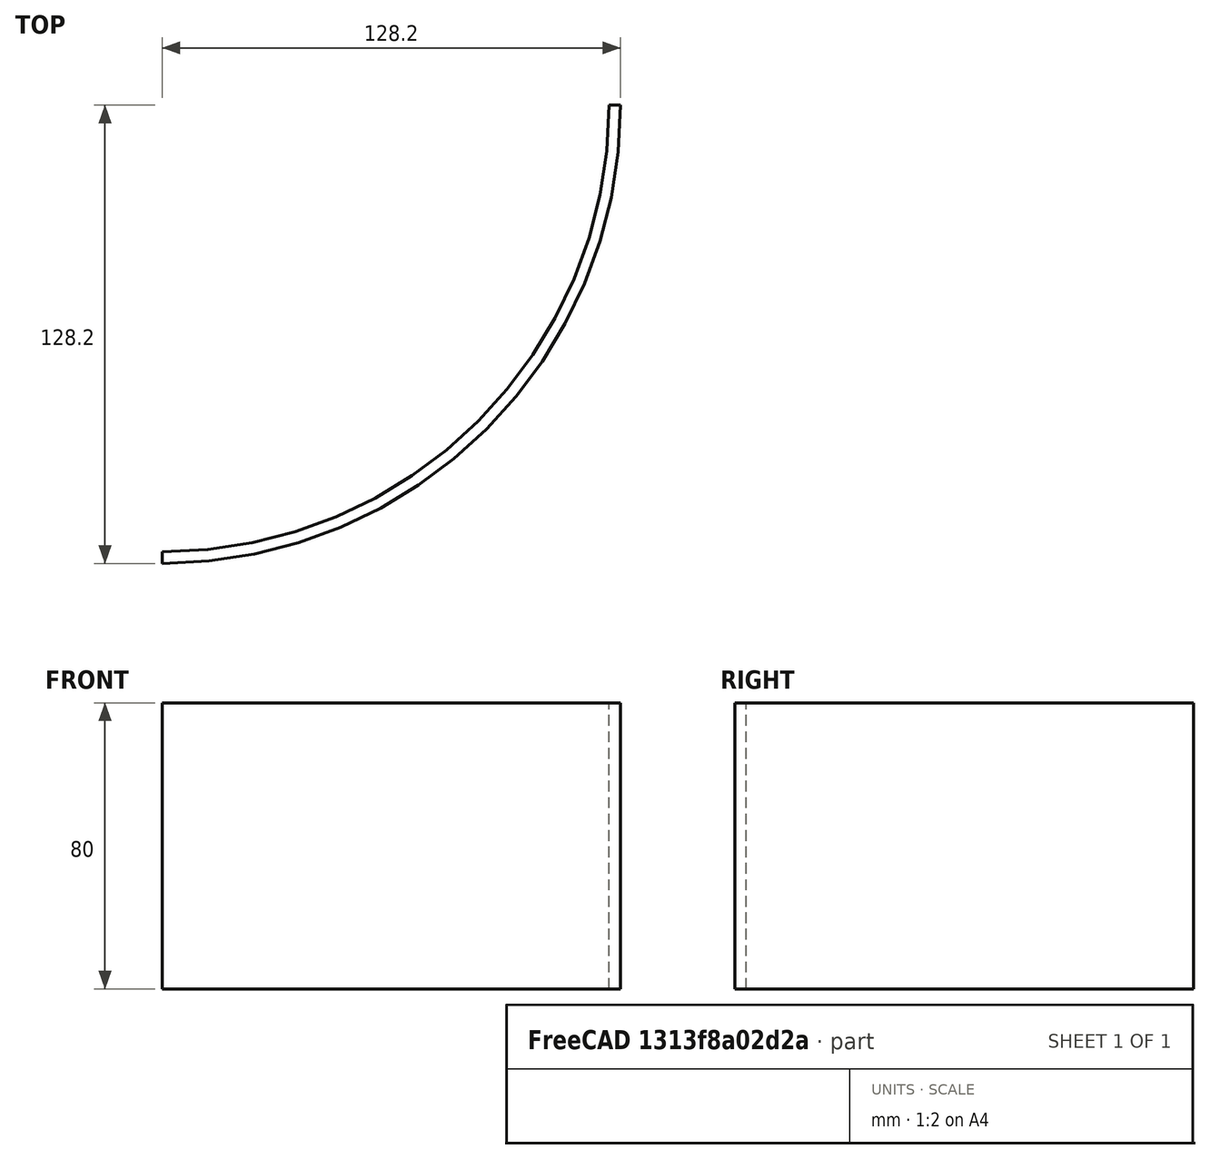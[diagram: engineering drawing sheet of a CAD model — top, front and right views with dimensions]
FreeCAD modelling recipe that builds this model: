
FCSTD DOCUMENT  (FreeCAD 0.20R29603 (Git))
Label: Concrete Weight Mold
License: All rights reserved
LicenseURL: http://en.wikipedia.org/wiki/All_rights_reserved
objects: Sketcher::SketchObject×1, Spreadsheet::Sheet×1, PartDesign::Pad×1, PartDesign::Body×1, App::Part×1
note: 4 computed .brp shape members not serialized (recipe doc carries the construction recipe); baked Part::Feature solids carry a one-line shape summary decoded from their .brp

FEATURE [Sketcher::SketchObject] Sketch
  FullyConstrained = true
  MapMode = 5
  Support = -> [XY_Plane001]
  expr: Constraints[10] = Spreadsheet.thickness
  expr: Constraints[8] = Spreadsheet.diameter / 2
  expr: Constraints[9] = Spreadsheet.diameter / 2 + Spreadsheet.thickness
  sketch-geometry (4):
    g0: ArcOfCircle CenterX=-4.71e-14 CenterY=-6.28e-14 CenterZ=0 NormalX=0 NormalY=0 NormalZ=1 AngleXU=0 Radius=125 StartAngle=4.71239 EndAngle=6.28319
    g1: ArcOfCircle CenterX=-4.71e-14 CenterY=-6.28e-14 CenterZ=0 NormalX=0 NormalY=0 NormalZ=1 AngleXU=0 Radius=128.2 StartAngle=4.71239 EndAngle=6.28319
    g2: LineSegment StartX=125 StartY=1.34436e-05 StartZ=0 EndX=128.2 EndY=-6.28e-14 EndZ=0
    g3: LineSegment StartX=-4.71e-14 StartY=-125 StartZ=0 EndX=-4.71e-14 EndY=-128.2 EndZ=0
  constraints (12):
    c: Coincident(g0,g-1)
    c: Coincident(g1,g0)
    c: Coincident(g2,g0)
    c: Coincident(g2,g1)
    c: Coincident(g3,g0)
    c: Coincident(g3,g1)
    c: Vertical(g0,g0)
    c: Vertical(g1,g0)
    c: Distance(g0,g0) = 125
    c: Distance(g0,g1) = 128.2
    c: Distance(g0,g1) = 3.2
    c: Horizontal(g0,g1)
FEATURE [Spreadsheet::Sheet] Spreadsheet
  cells = A1=diameter; B1(diameter)=250; A2=thickness; B2(thickness)=3.2; A3=height; B3(height)=80; A4=connector_thickness; B4(connector_thickness)=1.6; A5=connector_width; B5(connector_width)=100
FEATURE [PartDesign::Pad] Pad
  Direction = (0,0,1)
  Length = 80
  Length2 = 10
  Profile = -> Sketch
  ReferenceAxis = -> Sketch [N_Axis]
  Type = 0
  expr: Length = Spreadsheet.height
FEATURE [PartDesign::Body] Body
  Group = -> [Sketch,Pad]
  Origin = -> Origin001
  Tip = -> Pad
FEATURE [App::Part] Part  label="Quarter Mold"
  Group = -> [Body]
  Origin = -> Origin
